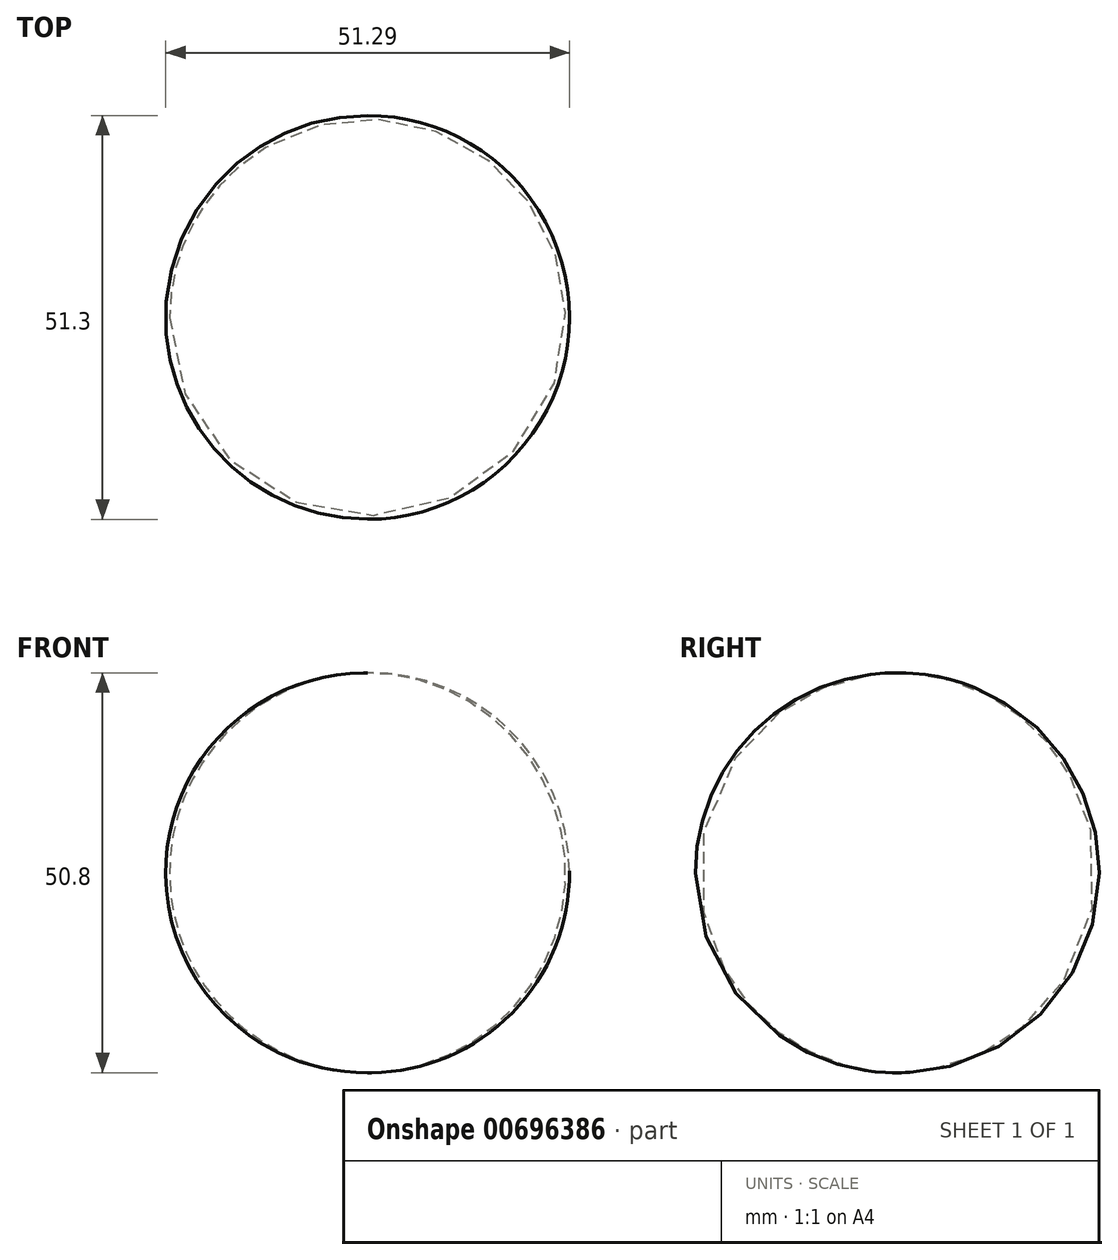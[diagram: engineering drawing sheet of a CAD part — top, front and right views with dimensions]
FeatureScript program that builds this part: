
annotation { "Feature Type Name" : "Feature", "Feature Type Description" : "" }
export const myFeature = defineFeature(function(context is Context, id is Id, definition is map)
    precondition{}
    {
        {
            var Q0;
            Q0=qCreatedBy(makeId("Front.planeOp"),FACE);
            var sketch = newSketch(context, id + "F0", { "sketchPlane" : qUnion([Q0])});
            skArc(sketch, "E0", {"start": v(0, -25.4) * mm, "mid": v(25.4, 0.25) * mm, "end": v(-0.5, 25.4) * mm});
            skLineSegment(sketch, "E1", {"start": v(-0.5, 25.4) * mm, "end": v(0, -25.4) * mm});
            skSolve(sketch);
        }
        {
            var Q0;
            Q0=makeQuery(id+"F0.imprint","IMPRINT",FACE,{"disambiguationData":[TD([[makeQuery(id+"F0.imprint","IMPRINT",EDGE,{"derivedFrom":sQuery(id+"F0.wireOp",EDGE,"E0")}),1.0]])]});
            var Q1;
            Q1=sQuery(id+"F0.wireOp",EDGE,"E1");
            revolve(context, id + "F1", {"entities" : qUnion([Q0]), "axis" : qUnion([Q1]), "revolveType" : RevolveType.FULL});
        }
    });
